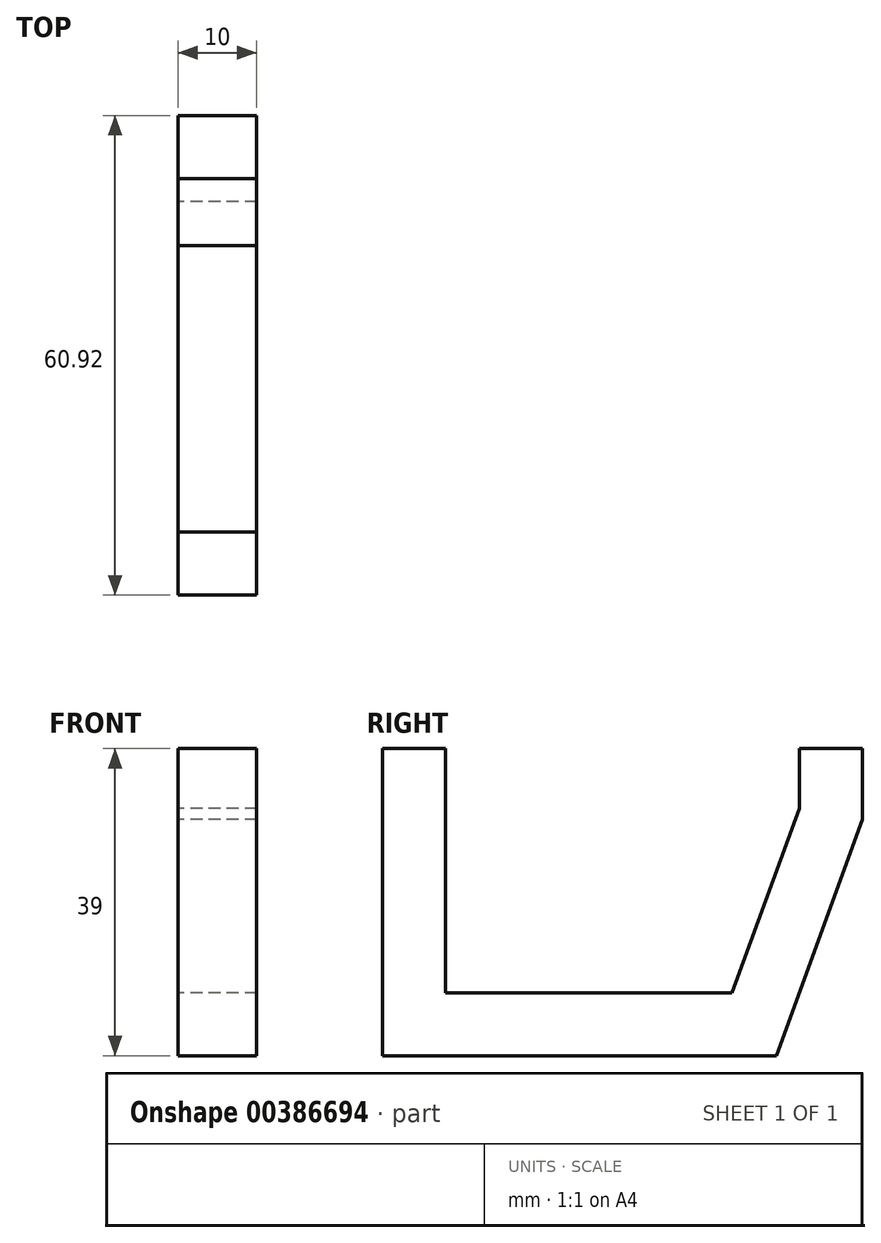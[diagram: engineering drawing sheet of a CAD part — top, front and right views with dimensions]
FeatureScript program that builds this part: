
annotation { "Feature Type Name" : "Feature", "Feature Type Description" : "" }
export const myFeature = defineFeature(function(context is Context, id is Id, definition is map)
    precondition{}
    {
        {
            var Q0;
            Q0=qCreatedBy(makeId("Right.planeOp"),FACE);
            var sketch = newSketch(context, id + "F0", { "sketchPlane" : qUnion([Q0])});
            skLineSegment(sketch, "E0", {"start": v(0, 0) * mm, "end": v(0, -30) * mm});
            skLineSegment(sketch, "E1", {"start": v(0, -30) * mm, "end": v(50, -30) * mm});
            skPoint(sketch, "E2.end.orphan", {"position": v(50, 0) * mm});
            skLineSegment(sketch, "E3", {"start": v(50, -30) * mm, "end": v(57.76, -8.67) * mm});
            skLineSegment(sketch, "E4", {"start": v(57.76, -8.67) * mm, "end": v(60.92, 0) * mm});
            skLineSegment(sketch, "E5", {"start": v(60.92, 0) * mm, "end": v(60.92, 9) * mm});
            skLineSegment(sketch, "E6", {"start": v(0, 0) * mm, "end": v(0, 9) * mm});
            skLineSegment(sketch, "E7.0", {"start": v(52.92, 1.41) * mm, "end": v(52.92, 9) * mm});
            skLineSegment(sketch, "E7.1", {"start": v(50.25, -5.93) * mm, "end": v(52.92, 1.41) * mm});
            skLineSegment(sketch, "E7.2", {"start": v(8, 0) * mm, "end": v(8, 9) * mm});
            skLineSegment(sketch, "E7.3", {"start": v(8, 0) * mm, "end": v(8, -22) * mm});
            skLineSegment(sketch, "E7.4", {"start": v(8, -22) * mm, "end": v(44.4, -22) * mm});
            skLineSegment(sketch, "E7.5", {"start": v(44.4, -22) * mm, "end": v(50.25, -5.93) * mm});
            skLineSegment(sketch, "E8", {"start": v(0, 9) * mm, "end": v(8, 9) * mm});
            skLineSegment(sketch, "E9", {"start": v(52.92, 9) * mm, "end": v(60.92, 9) * mm});
            skLineSegment(sketch, "E10", {"start": v(0, 9) * mm, "end": v(60.92, 9) * mm, "construction": true});
            skSolve(sketch);
        }
        {
            var Q0;
            Q0 = qSketchRegion(id + "F0", true);
            extrude(context, id + "F1", {"entities" : qUnion([Q0]), "depth" : 10 * mm});
        }
    });
